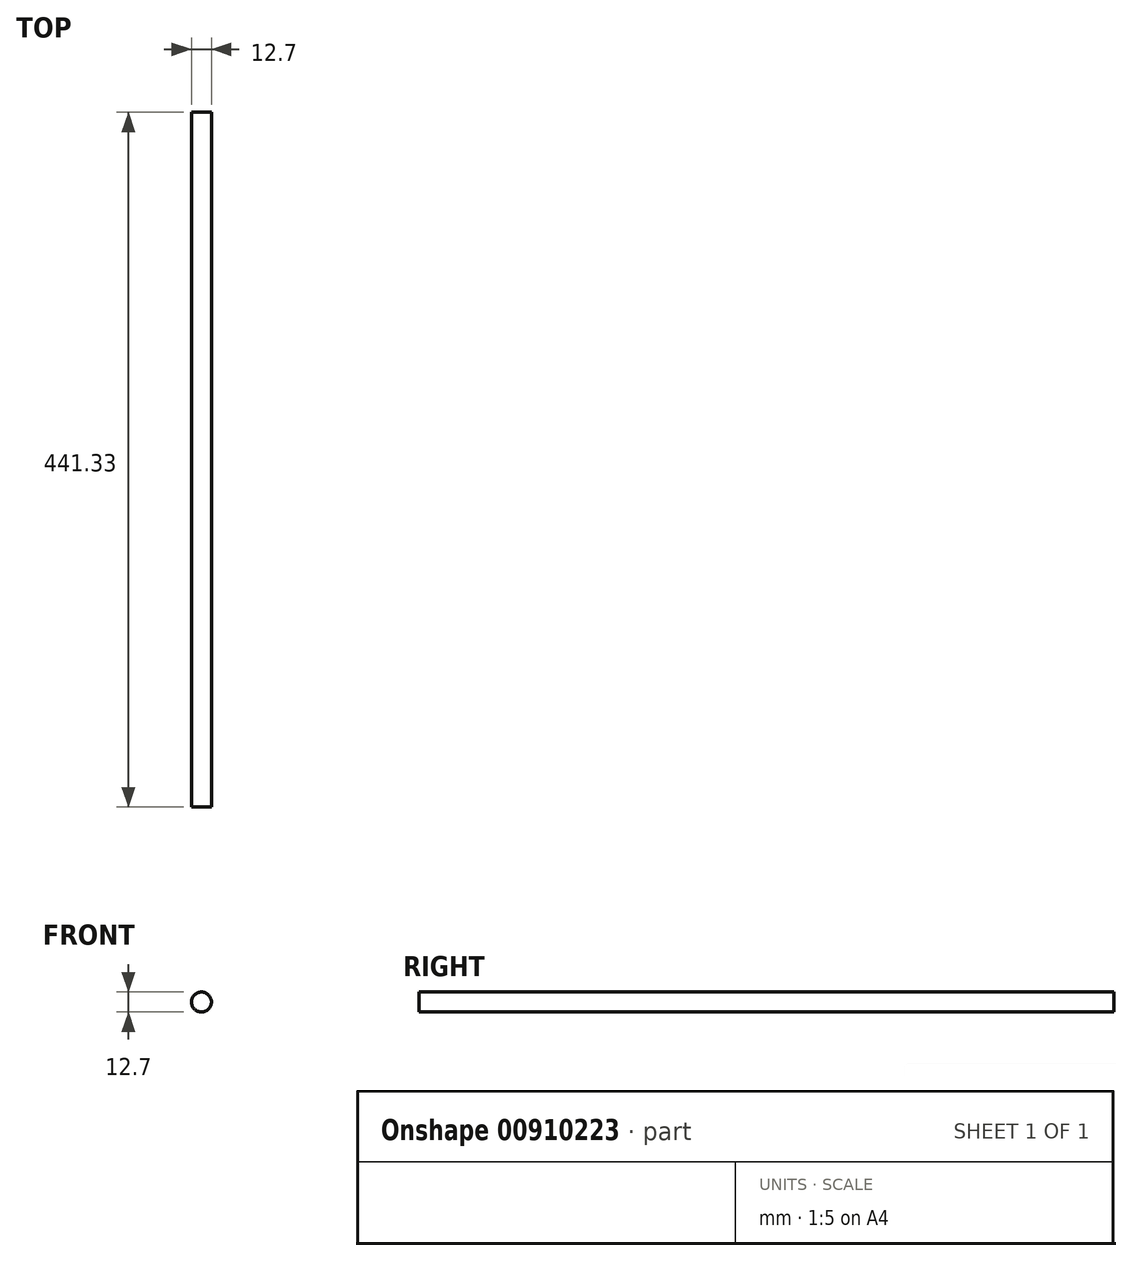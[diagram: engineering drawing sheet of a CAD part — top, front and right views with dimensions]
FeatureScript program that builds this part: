
annotation { "Feature Type Name" : "Feature", "Feature Type Description" : "" }
export const myFeature = defineFeature(function(context is Context, id is Id, definition is map)
    precondition{}
    {
        {
            var Q0;
            Q0=qCreatedBy(makeId("Front.planeOp"),FACE);
            var sketch = newSketch(context, id + "F0", { "sketchPlane" : qUnion([Q0])});
            skCircle(sketch, "E0", {"center": v(0, 0) * mm, "radius": 6.35 * mm});
            skSolve(sketch);
        }
        {
            var Q0;
            Q0=qSketchRegion(id+"F0",true);
            extrude(context, id + "F1", {"entities" : qUnion([Q0]), "depth" : 441.32 * mm, "offsetDistance" : 25.4 * mm});
        }
    });
